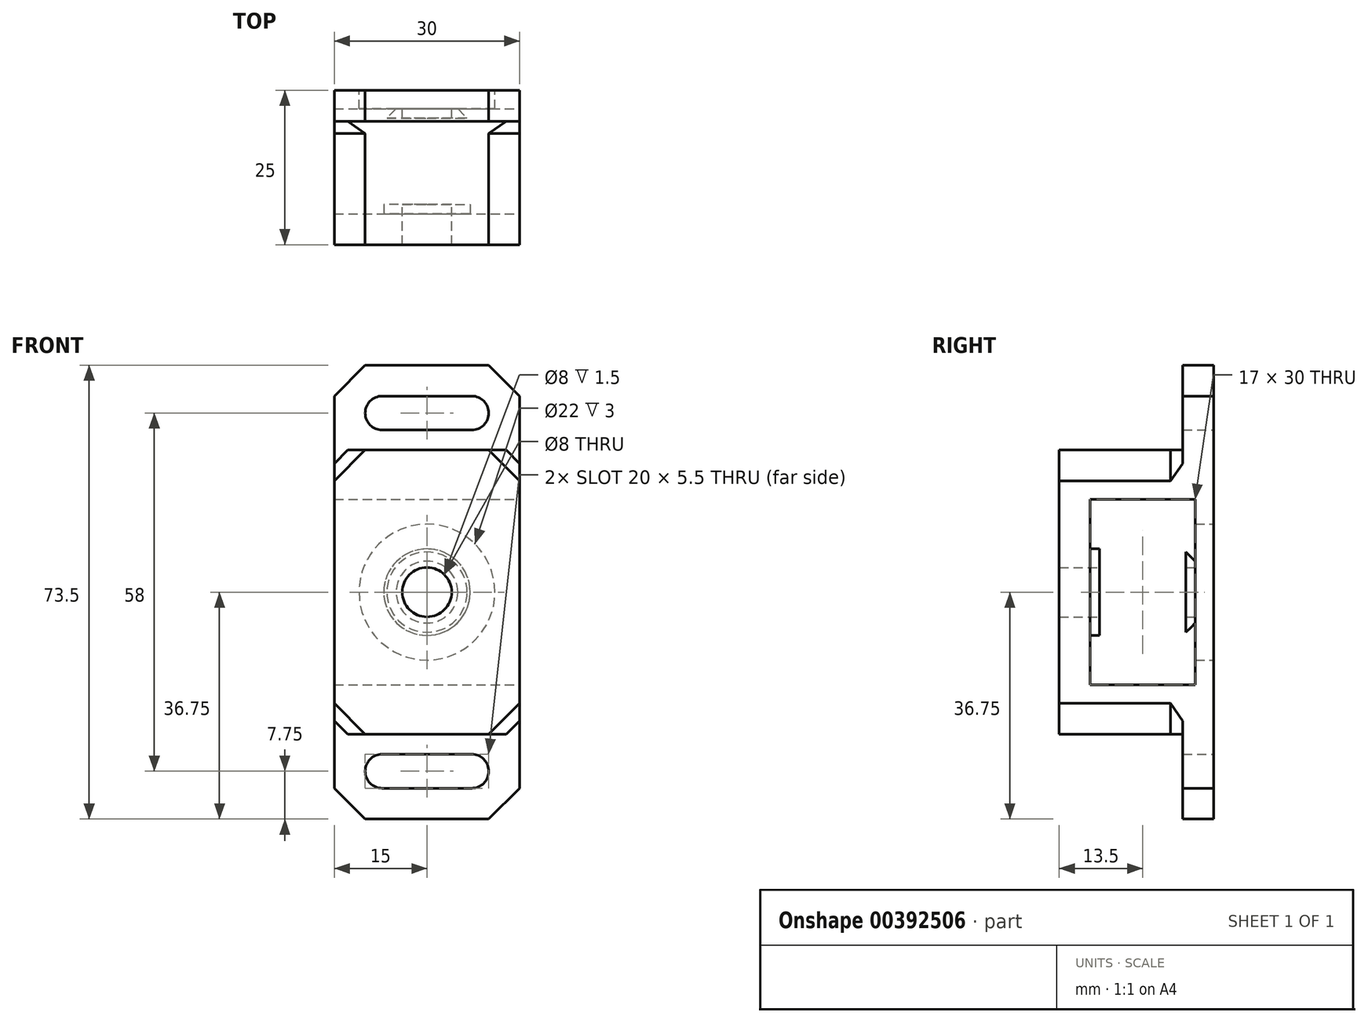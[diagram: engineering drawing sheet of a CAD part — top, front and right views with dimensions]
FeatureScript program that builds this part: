
annotation { "Feature Type Name" : "Feature", "Feature Type Description" : "" }
export const myFeature = defineFeature(function(context is Context, id is Id, definition is map)
    precondition{}
    {
        {
            var Q0;
            Q0=qCreatedBy(makeId("Front.planeOp"),FACE);
            var sketch = newSketch(context, id + "F0", { "sketchPlane" : qUnion([Q0])});
            skCircle(sketch, "E0", {"center": v(0, 0) * mm, "radius": 11 * mm});
            skCircle(sketch, "E1", {"center": v(0, 0) * mm, "radius": 4 * mm});
            skArc(sketch, "E2", {"start": v(-7.25, 31.75) * mm, "mid": v(-10, 29) * mm, "end": v(-7.25, 26.25) * mm});
            skCircle(sketch, "E3", {"center": v(0, 0) * mm, "radius": 15 * mm, "construction": true});
            skLineSegment(sketch, "E4", {"start": v(0, 0) * mm, "end": v(0, 36.75) * mm, "construction": true});
            skLineSegment(sketch, "E5.bottom", {"start": v(-15, 15) * mm, "end": v(15, 15) * mm});
            skLineSegment(sketch, "E5.top", {"start": v(-15, 23) * mm, "end": v(15, 23) * mm});
            skLineSegment(sketch, "E5.left", {"start": v(-15, 15) * mm, "end": v(-15, 23) * mm});
            skLineSegment(sketch, "E5.right", {"start": v(15, 15) * mm, "end": v(15, 23) * mm});
            skPoint(sketch, "E5.middle", {"position": v(0, 19) * mm});
            skArc(sketch, "E6", {"start": v(-1.92, 31.75) * mm, "mid": v(-13.25, 29) * mm, "end": v(-1.92, 26.25) * mm, "construction": true});
            skLineSegment(sketch, "E7", {"start": v(-15, 23) * mm, "end": v(-15, 36.75) * mm});
            skLineSegment(sketch, "E8", {"start": v(-15, 36.75) * mm, "end": v(0, 36.75) * mm});
            skPoint(sketch, "E9", {"position": v(-7.25, 31.75) * mm});
            skLineSegment(sketch, "E10", {"start": v(-7.25, 29) * mm, "end": v(-15, 29) * mm, "construction": true});
            skLineSegment(sketch, "E11", {"start": v(-7.25, 29) * mm, "end": v(-7.25, 36.75) * mm, "construction": true});
            skArc(sketch, "E12.MirrorC", {"start": v(7.25, 31.75) * mm, "mid": v(10, 29) * mm, "end": v(7.25, 26.25) * mm});
            skArc(sketch, "E13.MirrorC", {"start": v(1.92, 31.75) * mm, "mid": v(13.25, 29) * mm, "end": v(1.92, 26.25) * mm, "construction": true});
            skLineSegment(sketch, "E14.MirrorCS", {"start": v(15, 36.75) * mm, "end": v(0, 36.75) * mm});
            skLineSegment(sketch, "E15.MirrorCS", {"start": v(15, 23) * mm, "end": v(15, 36.75) * mm});
            skLineSegment(sketch, "E16", {"start": v(-7.25, 31.75) * mm, "end": v(7.25, 31.75) * mm});
            skLineSegment(sketch, "E17", {"start": v(-7.25, 26.25) * mm, "end": v(7.25, 26.25) * mm});
            skLineSegment(sketch, "E18", {"start": v(-15, 15) * mm, "end": v(-15, 0) * mm});
            skLineSegment(sketch, "E19", {"start": v(15, 15) * mm, "end": v(15, 0) * mm});
            skLineSegment(sketch, "E20", {"start": v(0, 0) * mm, "end": v(15, 0) * mm, "construction": true});
            skLineSegment(sketch, "E21.MirrorCS", {"start": v(-7.25, -29) * mm, "end": v(-7.25, -36.75) * mm, "construction": true});
            skPoint(sketch, "E22.MirrorP", {"position": v(-7.25, -31.75) * mm});
            skLineSegment(sketch, "E23.MirrorCS", {"start": v(-15, -15) * mm, "end": v(-15, 0) * mm});
            skLineSegment(sketch, "E24.MirrorCS", {"start": v(15, -15) * mm, "end": v(15, 0) * mm});
            skPoint(sketch, "E25.MirrorP", {"position": v(0, -19) * mm});
            skLineSegment(sketch, "E26.MirrorCS", {"start": v(-7.25, -29) * mm, "end": v(-15, -29) * mm, "construction": true});
            skLineSegment(sketch, "E27.MirrorCS", {"start": v(-15, -36.75) * mm, "end": v(0, -36.75) * mm});
            skLineSegment(sketch, "E28.MirrorCS", {"start": v(-7.25, -26.25) * mm, "end": v(7.25, -26.25) * mm});
            skLineSegment(sketch, "E29.MirrorCS", {"start": v(15, -36.75) * mm, "end": v(0, -36.75) * mm});
            skLineSegment(sketch, "E30.MirrorCS", {"start": v(-7.25, -31.75) * mm, "end": v(7.25, -31.75) * mm});
            skLineSegment(sketch, "E31.MirrorCS", {"start": v(-15, -15) * mm, "end": v(-15, -23) * mm});
            skLineSegment(sketch, "E32.MirrorCS", {"start": v(15, -15) * mm, "end": v(15, -23) * mm});
            skArc(sketch, "E33.MirrorCS", {"start": v(1.92, -31.75) * mm, "mid": v(13.25, -29) * mm, "end": v(1.92, -26.25) * mm, "construction": true});
            skLineSegment(sketch, "E34.MirrorCS", {"start": v(-15, -23) * mm, "end": v(15, -23) * mm});
            skLineSegment(sketch, "E35.MirrorCS", {"start": v(-15, -23) * mm, "end": v(-15, -36.75) * mm});
            skLineSegment(sketch, "E36.MirrorCS", {"start": v(15, -23) * mm, "end": v(15, -36.75) * mm});
            skArc(sketch, "E37.MirrorCS", {"start": v(-1.92, -31.75) * mm, "mid": v(-13.25, -29) * mm, "end": v(-1.92, -26.25) * mm, "construction": true});
            skLineSegment(sketch, "E38.MirrorCS", {"start": v(0, 0) * mm, "end": v(0, -36.75) * mm, "construction": true});
            skLineSegment(sketch, "E39.MirrorCS", {"start": v(-15, -15) * mm, "end": v(15, -15) * mm});
            skArc(sketch, "E40.MirrorCS", {"start": v(-7.25, -31.75) * mm, "mid": v(-10, -29) * mm, "end": v(-7.25, -26.25) * mm});
            skArc(sketch, "E41.MirrorCS", {"start": v(7.25, -31.75) * mm, "mid": v(10, -29) * mm, "end": v(7.25, -26.25) * mm});
            skSolve(sketch);
        }
        {
            var Q0;
            Q0=makeQuery(id+"F0.imprint","IMPRINT",FACE,{"disambiguationData":[TD([[makeQuery(id+"F0.imprint","IMPRINT",EDGE,{"derivedFrom":sQuery(id+"F0.wireOp",EDGE,"E5.bottom")}),-1.0]])]});
            var Q1;
            Q1=makeQuery(id+"F0.imprint","IMPRINT",FACE,{"disambiguationData":[TD([[makeQuery(id+"F0.imprint","IMPRINT",EDGE,{"derivedFrom":sQuery(id+"F0.wireOp",EDGE,"E0")}),-1.0]])]});
            extrude(context, id + "F1", {"entities" : qUnion([Q0, Q1]), "depth" : 3 * mm});
        }
        {
            var Q0;
            Q0=makeQuery(id+"F0.imprint","IMPRINT",FACE,{"disambiguationData":[TD([[makeQuery(id+"F0.imprint","IMPRINT",EDGE,{"derivedFrom":sQuery(id+"F0.wireOp",EDGE,"E5.bottom")}),1.0]])]});
            var Q1;
            Q1=makeQuery(id+"F0.imprint","IMPRINT",FACE,{"disambiguationData":[TD([[makeQuery(id+"F0.imprint","IMPRINT",EDGE,{"derivedFrom":sQuery(id+"F0.wireOp",EDGE,"E31.MirrorCS")}),1.0]])]});
            extrude(context, id + "F2", {"entities" : qUnion([Q0, Q1]), "operationType" : NewBodyOperationType.ADD, "depth" : 20 * mm});
        }
        {
            var Q0;
            Q0=makeQuery(id+"F0.imprint","IMPRINT",FACE,{"disambiguationData":[TD([[makeQuery(id+"F0.imprint","IMPRINT",EDGE,{"derivedFrom":sQuery(id+"F0.wireOp",EDGE,"E27.MirrorCS")}),1.0]])]});
            var Q1;
            Q1=makeQuery(id+"F0.imprint","IMPRINT",FACE,{"disambiguationData":[TD([[makeQuery(id+"F0.imprint","IMPRINT",EDGE,{"derivedFrom":sQuery(id+"F0.wireOp",EDGE,"E2")}),-1.0]])]});
            extrude(context, id + "F3", {"entities" : qUnion([Q0, Q1]), "operationType" : NewBodyOperationType.ADD, "depth" : 5 * mm});
        }
        {
            var Q0;
            Q0=makeQuery(id+"F2.opExtrude","CAP_FACE",FACE,{"disambiguationData":[OSD([sQuery(id+"F0.wireOp",EDGE,"E5.bottom"),sQuery(id+"F0.wireOp",EDGE,"E5.top"),sQuery(id+"F0.wireOp",EDGE,"E5.left"),sQuery(id+"F0.wireOp",EDGE,"E5.right")])],"isStart":false});
            var sketch = newSketch(context, id + "F4", { "sketchPlane" : qUnion([Q0])});
            skLineSegment(sketch, "E42.bottom", {"start": v(-15, 23) * mm, "end": v(15, 23) * mm});
            skLineSegment(sketch, "E42.top", {"start": v(-15, -23) * mm, "end": v(15, -23) * mm});
            skLineSegment(sketch, "E42.left", {"start": v(-15, 23) * mm, "end": v(-15, -23) * mm});
            skLineSegment(sketch, "E42.right", {"start": v(15, 23) * mm, "end": v(15, -23) * mm});
            skCircle(sketch, "E43", {"center": v(0, 0) * mm, "radius": 4 * mm});
            skSolve(sketch);
        }
        {
            var Q0;
            Q0 = qSketchRegion(id + "F4", true);
            extrude(context, id + "F5", {"entities" : qUnion([Q0]), "operationType" : NewBodyOperationType.ADD, "depth" : 5 * mm});
        }
        {
            var Q0;
            Q0=makeQuery(id+"F1.opExtrude","CAP_FACE",FACE,{"disambiguationData":[OSD([sQuery(id+"F0.wireOp",EDGE,"E5.bottom"),sQuery(id+"F0.wireOp",EDGE,"E18"),sQuery(id+"F0.wireOp",EDGE,"E19"),sQuery(id+"F0.wireOp",EDGE,"E23.MirrorCS"),sQuery(id+"F0.wireOp",EDGE,"E24.MirrorCS"),sQuery(id+"F0.wireOp",EDGE,"E39.MirrorCS"),sQuery(id+"F0.wireOp",EDGE,"E1")])],"isStart":false});
            var sketch = newSketch(context, id + "F6", { "sketchPlane" : qUnion([Q0])});
            skCircle(sketch, "E44", {"center": v(0, 0) * mm, "radius": 7 * mm});
            skCircle(sketch, "E45", {"center": v(0, 0) * mm, "radius": 4 * mm});
            skSolve(sketch);
        }
        {
            var Q0;
            Q0 = qSketchRegion(id + "F6", true);
            extrude(context, id + "F7", {"entities" : qUnion([Q0]), "operationType" : NewBodyOperationType.ADD, "depth" : 1.5 * mm});
        }
        {
            var Q0;
            Q0=makeQuery(id+"F5.opExtrude","CAP_FACE",FACE,{"disambiguationData":[OSD([sQuery(id+"F4.wireOp",EDGE,"E42.bottom"),sQuery(id+"F4.wireOp",EDGE,"E42.top"),sQuery(id+"F4.wireOp",EDGE,"E42.left"),sQuery(id+"F4.wireOp",EDGE,"E42.right"),sQuery(id+"F4.wireOp",EDGE,"E43")])],"isStart":true});
            var sketch = newSketch(context, id + "F8", { "sketchPlane" : qUnion([Q0])});
            skCircle(sketch, "E46.0", {"center": v(0, 0) * mm, "radius": 4 * mm});
            skCircle(sketch, "E46.1", {"center": v(0, 0) * mm, "radius": 7 * mm});
            skSolve(sketch);
        }
        {
            var Q0;
            Q0 = qSketchRegion(id + "F8", true);
            extrude(context, id + "F9", {"entities" : qUnion([Q0]), "operationType" : NewBodyOperationType.ADD, "depth" : 1.5 * mm});
        }
        {
            var Q0;
            Q0=makeQuery(id+"F3.opExtrude","SWEPT_EDGE",EDGE,{"disambiguationData":[OSD([sQuery(id+"F0.wireOp",EDGE,"E14.MirrorCS"),sQuery(id+"F0.wireOp",EDGE,"E15.MirrorCS")])]});
            var Q1;
            Q1=makeQuery(id+"F3.opExtrude","SWEPT_EDGE",EDGE,{"disambiguationData":[OSD([sQuery(id+"F0.wireOp",EDGE,"E7"),sQuery(id+"F0.wireOp",EDGE,"E8")])]});
            var Q2;
            Q2=makeQuery(id+"F3.opExtrude","SWEPT_EDGE",EDGE,{"disambiguationData":[OSD([sQuery(id+"F0.wireOp",EDGE,"E29.MirrorCS"),sQuery(id+"F0.wireOp",EDGE,"E36.MirrorCS")])]});
            var Q3;
            Q3=makeQuery(id+"F3.opExtrude","SWEPT_EDGE",EDGE,{"disambiguationData":[OSD([sQuery(id+"F0.wireOp",EDGE,"E27.MirrorCS"),sQuery(id+"F0.wireOp",EDGE,"E35.MirrorCS")])]});
            var Q4;
            Q4=makeQuery(id+"F5.boolean.opBoolean","MERGE",EDGE,{"derivedFrom":[makeQuery(id+"F2.opExtrude","SWEPT_EDGE",EDGE,{"disambiguationData":[OSD([sQuery(id+"F0.wireOp",EDGE,"E5.top"),sQuery(id+"F0.wireOp",EDGE,"E5.left"),sQuery(id+"F0.wireOp",EDGE,"E7")])]}),makeQuery(id+"F5.opExtrude","SWEPT_EDGE",EDGE,{"disambiguationData":[OSD([sQuery(id+"F4.wireOp",EDGE,"E42.bottom"),sQuery(id+"F4.wireOp",EDGE,"E42.left")])]})]});
            var Q5;
            Q5=makeQuery(id+"F5.boolean.opBoolean","MERGE",EDGE,{"derivedFrom":[makeQuery(id+"F2.opExtrude","SWEPT_EDGE",EDGE,{"disambiguationData":[OSD([sQuery(id+"F0.wireOp",EDGE,"E5.top"),sQuery(id+"F0.wireOp",EDGE,"E5.right"),sQuery(id+"F0.wireOp",EDGE,"E15.MirrorCS")])]}),makeQuery(id+"F5.opExtrude","SWEPT_EDGE",EDGE,{"disambiguationData":[OSD([sQuery(id+"F4.wireOp",EDGE,"E42.bottom"),sQuery(id+"F4.wireOp",EDGE,"E42.right")])]})]});
            var Q6;
            Q6=makeQuery(id+"F5.boolean.opBoolean","MERGE",EDGE,{"derivedFrom":[makeQuery(id+"F2.opExtrude","SWEPT_EDGE",EDGE,{"disambiguationData":[OSD([sQuery(id+"F0.wireOp",EDGE,"E32.MirrorCS"),sQuery(id+"F0.wireOp",EDGE,"E34.MirrorCS"),sQuery(id+"F0.wireOp",EDGE,"E36.MirrorCS")])]}),makeQuery(id+"F5.opExtrude","SWEPT_EDGE",EDGE,{"disambiguationData":[OSD([sQuery(id+"F4.wireOp",EDGE,"E42.top"),sQuery(id+"F4.wireOp",EDGE,"E42.right")])]})]});
            var Q7;
            Q7=makeQuery(id+"F5.boolean.opBoolean","MERGE",EDGE,{"derivedFrom":[makeQuery(id+"F2.opExtrude","SWEPT_EDGE",EDGE,{"disambiguationData":[OSD([sQuery(id+"F0.wireOp",EDGE,"E31.MirrorCS"),sQuery(id+"F0.wireOp",EDGE,"E34.MirrorCS"),sQuery(id+"F0.wireOp",EDGE,"E35.MirrorCS")])]}),makeQuery(id+"F5.opExtrude","SWEPT_EDGE",EDGE,{"disambiguationData":[OSD([sQuery(id+"F4.wireOp",EDGE,"E42.top"),sQuery(id+"F4.wireOp",EDGE,"E42.left")])]})]});
            chamfer(context, id + "F10", {"entities" : qUnion([Q0, Q1, Q2, Q3, Q4, Q5, Q6, Q7]), "width" : 5 * mm, "tangentPropagation" : true});
        }
        {
            var Q0;
            Q0=makeQuery(id+"F7.opExtrude","CAP_EDGE",EDGE,{"disambiguationData":[OSD([sQuery(id+"F6.wireOp",EDGE,"E44")])],"isStart":true});
            var Q1;
            Q1=makeQuery(id+"F9.opExtrude","CAP_EDGE",EDGE,{"disambiguationData":[OSD([sQuery(id+"F8.wireOp",EDGE,"E46.1")])],"isStart":true});
            chamfer(context, id + "F11", {"entities" : qUnion([Q0, Q1]), "width" : 2 * mm, "tangentPropagation" : true});
        }
        {
            var Q0;
            {var subQ0=sQuery(id+"F0.wireOp",EDGE,"E15.MirrorCS");var subQ1=sQuery(id+"F0.wireOp",EDGE,"E5.top");Q0=makeQuery(id+"F10.opChamfer","BLEND_EDGE",EDGE,{"blendedFrom":[makeQuery(id+"F5.boolean.opBoolean","MERGE",EDGE,{"derivedFrom":[makeQuery(id+"F2.opExtrude","SWEPT_EDGE",EDGE,{"disambiguationData":[OSD([subQ1,sQuery(id+"F0.wireOp",EDGE,"E5.right"),subQ0])]}),makeQuery(id+"F5.opExtrude","SWEPT_EDGE",EDGE,{"disambiguationData":[OSD([sQuery(id+"F4.wireOp",EDGE,"E42.bottom"),sQuery(id+"F4.wireOp",EDGE,"E42.right")])]})]}),makeQuery(id+"F3.opExtrude","CAP_FACE",FACE,{"disambiguationData":[OSD([sQuery(id+"F0.wireOp",EDGE,"E2"),subQ1,sQuery(id+"F0.wireOp",EDGE,"E7"),sQuery(id+"F0.wireOp",EDGE,"E8"),sQuery(id+"F0.wireOp",EDGE,"E12.MirrorC"),sQuery(id+"F0.wireOp",EDGE,"E14.MirrorCS"),subQ0,sQuery(id+"F0.wireOp",EDGE,"E16"),sQuery(id+"F0.wireOp",EDGE,"E17")])],"isStart":false})],"blendedInto":[makeQuery(id+"F3.opExtrude","CAP_FACE",FACE,{"disambiguationData":[OSD([sQuery(id+"F0.wireOp",EDGE,"E2"),subQ1,sQuery(id+"F0.wireOp",EDGE,"E7"),sQuery(id+"F0.wireOp",EDGE,"E8"),sQuery(id+"F0.wireOp",EDGE,"E12.MirrorC"),sQuery(id+"F0.wireOp",EDGE,"E14.MirrorCS"),subQ0,sQuery(id+"F0.wireOp",EDGE,"E16"),sQuery(id+"F0.wireOp",EDGE,"E17")])],"isStart":false})]});}
            var Q1;
            {var subQ0=sQuery(id+"F0.wireOp",EDGE,"E7");var subQ1=sQuery(id+"F0.wireOp",EDGE,"E5.top");Q1=makeQuery(id+"F10.opChamfer","BLEND_EDGE",EDGE,{"blendedFrom":[makeQuery(id+"F5.boolean.opBoolean","MERGE",EDGE,{"derivedFrom":[makeQuery(id+"F2.opExtrude","SWEPT_EDGE",EDGE,{"disambiguationData":[OSD([subQ1,sQuery(id+"F0.wireOp",EDGE,"E5.left"),subQ0])]}),makeQuery(id+"F5.opExtrude","SWEPT_EDGE",EDGE,{"disambiguationData":[OSD([sQuery(id+"F4.wireOp",EDGE,"E42.bottom"),sQuery(id+"F4.wireOp",EDGE,"E42.left")])]})]}),makeQuery(id+"F3.opExtrude","CAP_FACE",FACE,{"disambiguationData":[OSD([sQuery(id+"F0.wireOp",EDGE,"E2"),subQ1,subQ0,sQuery(id+"F0.wireOp",EDGE,"E8"),sQuery(id+"F0.wireOp",EDGE,"E12.MirrorC"),sQuery(id+"F0.wireOp",EDGE,"E14.MirrorCS"),sQuery(id+"F0.wireOp",EDGE,"E15.MirrorCS"),sQuery(id+"F0.wireOp",EDGE,"E16"),sQuery(id+"F0.wireOp",EDGE,"E17")])],"isStart":false})],"blendedInto":[makeQuery(id+"F3.opExtrude","CAP_FACE",FACE,{"disambiguationData":[OSD([sQuery(id+"F0.wireOp",EDGE,"E2"),subQ1,subQ0,sQuery(id+"F0.wireOp",EDGE,"E8"),sQuery(id+"F0.wireOp",EDGE,"E12.MirrorC"),sQuery(id+"F0.wireOp",EDGE,"E14.MirrorCS"),sQuery(id+"F0.wireOp",EDGE,"E15.MirrorCS"),sQuery(id+"F0.wireOp",EDGE,"E16"),sQuery(id+"F0.wireOp",EDGE,"E17")])],"isStart":false})]});}
            var Q2;
            {var subQ0=sQuery(id+"F0.wireOp",EDGE,"E35.MirrorCS");var subQ1=sQuery(id+"F0.wireOp",EDGE,"E34.MirrorCS");Q2=makeQuery(id+"F10.opChamfer","BLEND_EDGE",EDGE,{"blendedFrom":[makeQuery(id+"F5.boolean.opBoolean","MERGE",EDGE,{"derivedFrom":[makeQuery(id+"F2.opExtrude","SWEPT_EDGE",EDGE,{"disambiguationData":[OSD([sQuery(id+"F0.wireOp",EDGE,"E31.MirrorCS"),subQ1,subQ0])]}),makeQuery(id+"F5.opExtrude","SWEPT_EDGE",EDGE,{"disambiguationData":[OSD([sQuery(id+"F4.wireOp",EDGE,"E42.top"),sQuery(id+"F4.wireOp",EDGE,"E42.left")])]})]}),makeQuery(id+"F3.opExtrude","CAP_FACE",FACE,{"disambiguationData":[OSD([sQuery(id+"F0.wireOp",EDGE,"E27.MirrorCS"),sQuery(id+"F0.wireOp",EDGE,"E28.MirrorCS"),sQuery(id+"F0.wireOp",EDGE,"E29.MirrorCS"),sQuery(id+"F0.wireOp",EDGE,"E30.MirrorCS"),subQ1,subQ0,sQuery(id+"F0.wireOp",EDGE,"E36.MirrorCS"),sQuery(id+"F0.wireOp",EDGE,"E40.MirrorCS"),sQuery(id+"F0.wireOp",EDGE,"E41.MirrorCS")])],"isStart":false})],"blendedInto":[makeQuery(id+"F3.opExtrude","CAP_FACE",FACE,{"disambiguationData":[OSD([sQuery(id+"F0.wireOp",EDGE,"E27.MirrorCS"),sQuery(id+"F0.wireOp",EDGE,"E28.MirrorCS"),sQuery(id+"F0.wireOp",EDGE,"E29.MirrorCS"),sQuery(id+"F0.wireOp",EDGE,"E30.MirrorCS"),subQ1,subQ0,sQuery(id+"F0.wireOp",EDGE,"E36.MirrorCS"),sQuery(id+"F0.wireOp",EDGE,"E40.MirrorCS"),sQuery(id+"F0.wireOp",EDGE,"E41.MirrorCS")])],"isStart":false})]});}
            var Q3;
            {var subQ0=sQuery(id+"F0.wireOp",EDGE,"E36.MirrorCS");var subQ1=sQuery(id+"F0.wireOp",EDGE,"E34.MirrorCS");Q3=makeQuery(id+"F10.opChamfer","BLEND_EDGE",EDGE,{"blendedFrom":[makeQuery(id+"F5.boolean.opBoolean","MERGE",EDGE,{"derivedFrom":[makeQuery(id+"F2.opExtrude","SWEPT_EDGE",EDGE,{"disambiguationData":[OSD([sQuery(id+"F0.wireOp",EDGE,"E32.MirrorCS"),subQ1,subQ0])]}),makeQuery(id+"F5.opExtrude","SWEPT_EDGE",EDGE,{"disambiguationData":[OSD([sQuery(id+"F4.wireOp",EDGE,"E42.top"),sQuery(id+"F4.wireOp",EDGE,"E42.right")])]})]}),makeQuery(id+"F3.opExtrude","CAP_FACE",FACE,{"disambiguationData":[OSD([sQuery(id+"F0.wireOp",EDGE,"E27.MirrorCS"),sQuery(id+"F0.wireOp",EDGE,"E28.MirrorCS"),sQuery(id+"F0.wireOp",EDGE,"E29.MirrorCS"),sQuery(id+"F0.wireOp",EDGE,"E30.MirrorCS"),subQ1,sQuery(id+"F0.wireOp",EDGE,"E35.MirrorCS"),subQ0,sQuery(id+"F0.wireOp",EDGE,"E40.MirrorCS"),sQuery(id+"F0.wireOp",EDGE,"E41.MirrorCS")])],"isStart":false})],"blendedInto":[makeQuery(id+"F3.opExtrude","CAP_FACE",FACE,{"disambiguationData":[OSD([sQuery(id+"F0.wireOp",EDGE,"E27.MirrorCS"),sQuery(id+"F0.wireOp",EDGE,"E28.MirrorCS"),sQuery(id+"F0.wireOp",EDGE,"E29.MirrorCS"),sQuery(id+"F0.wireOp",EDGE,"E30.MirrorCS"),subQ1,sQuery(id+"F0.wireOp",EDGE,"E35.MirrorCS"),subQ0,sQuery(id+"F0.wireOp",EDGE,"E40.MirrorCS"),sQuery(id+"F0.wireOp",EDGE,"E41.MirrorCS")])],"isStart":false})]});}
            chamfer(context, id + "F12", {"entities" : qUnion([Q0, Q1, Q2, Q3]), "width" : 2 * mm, "tangentPropagation" : true});
        }
    });
